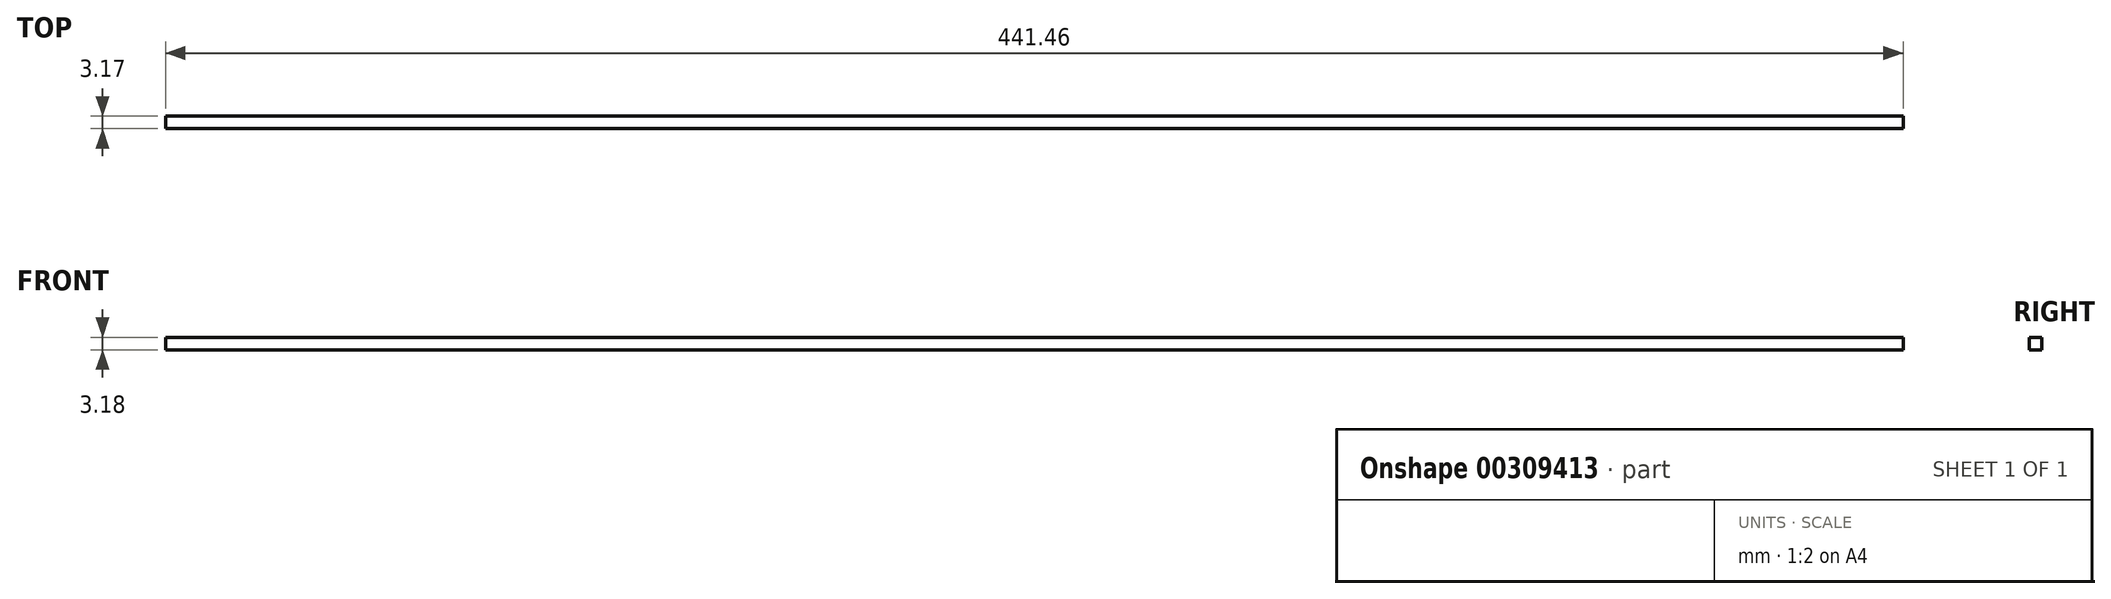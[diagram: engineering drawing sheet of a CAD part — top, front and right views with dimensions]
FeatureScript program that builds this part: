
annotation { "Feature Type Name" : "Feature", "Feature Type Description" : "" }
export const myFeature = defineFeature(function(context is Context, id is Id, definition is map)
    precondition{}
    {
        {
            var Q0;
            Q0=qCreatedBy(makeId("Front.planeOp"),FACE);
            var sketch = newSketch(context, id + "F0", { "sketchPlane" : qUnion([Q0])});
            skLineSegment(sketch, "E0.bottom", {"start": v(220.73, -1.59) * mm, "end": v(-220.73, -1.59) * mm});
            skLineSegment(sketch, "E0.top", {"start": v(220.73, 1.59) * mm, "end": v(-220.73, 1.59) * mm});
            skLineSegment(sketch, "E0.left", {"start": v(220.73, -1.59) * mm, "end": v(220.73, 1.59) * mm});
            skLineSegment(sketch, "E0.right", {"start": v(-220.73, -1.59) * mm, "end": v(-220.73, 1.59) * mm});
            skPoint(sketch, "E0.middle", {"position": v(0, 0) * mm});
            skSolve(sketch);
        }
        {
            var Q0;
            Q0=makeQuery(id+"F0.imprint","IMPRINT",FACE,{"disambiguationData":[TD([[makeQuery(id+"F0.imprint","IMPRINT",EDGE,{"derivedFrom":sQuery(id+"F0.wireOp",EDGE,"E0.bottom")}),-1.0]])]});
            extrude(context, id + "F1", {"entities" : qUnion([Q0]), "depth" : 3.17 * mm});
        }
    });
